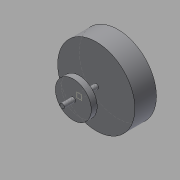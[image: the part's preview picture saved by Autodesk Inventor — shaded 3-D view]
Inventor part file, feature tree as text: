
AUTODESK INVENTOR PART (.ipt)
format: ipt  version: 2015 (Build 190159000, 159)  size: 90,112 bytes
history: native  units: mm
features: extrude x3, sketch x3, plane x1
ambient origin geometry x8: Origin, YZ Plane, XZ Plane, XY Plane, X Axis, Y Axis, Z Axis, Center Point
bodies: Solid1 (feature_tree)
feature tree (7):
  extrude  "Extrusion1"  Depth=12.0mm TaperAngle=0.0deg
  extrude  "Extrusion2"  Depth=19.0mm TaperAngle=0.0deg
  plane  "Work Plane1"
  extrude  "Extrusion3"  Depth=3.3mm
  sketch  "Sketch2"  dims[d0=43.0mm d1=12.0mm d2=0.0mm]
  sketch  "Sketch3"  dims[d3=2.5mm d4=19.0mm d5=0.0mm]
  sketch  "Sketch4"  dims[d6=-9.5mm d7=20.0mm d8=2.5mm d9=3.3mm d10=0.0mm]
